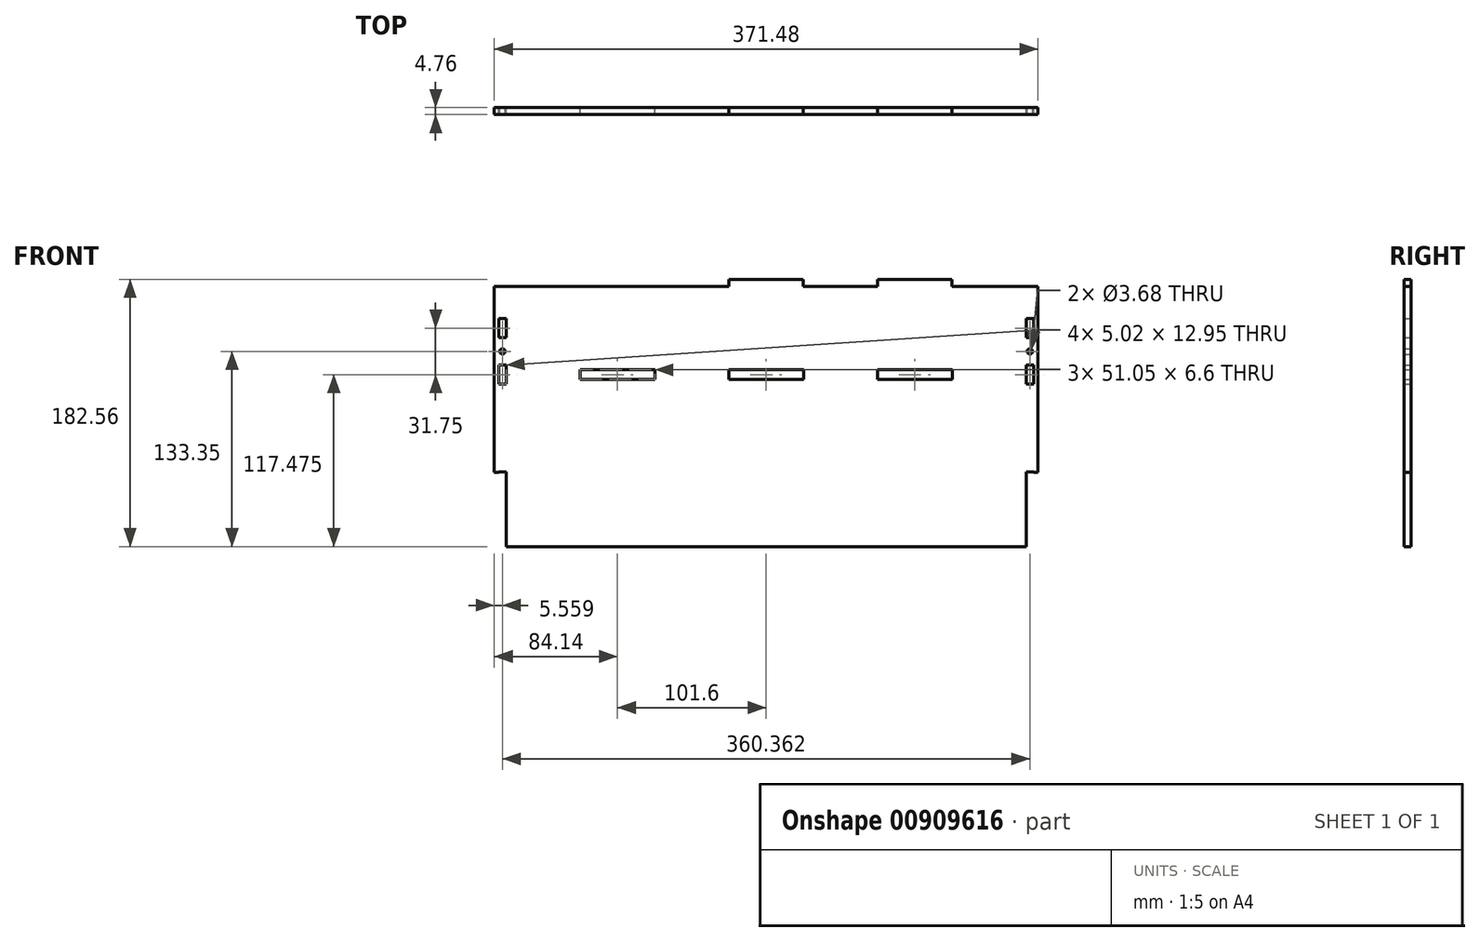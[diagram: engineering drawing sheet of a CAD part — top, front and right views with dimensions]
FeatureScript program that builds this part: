
annotation { "Feature Type Name" : "Feature", "Feature Type Description" : "" }
export const myFeature = defineFeature(function(context is Context, id is Id, definition is map)
    precondition{}
    {
        {
            var Q0;
            Q0=qCreatedBy(makeId("Front.planeOp"),FACE);
            var sketch = newSketch(context, id + "F0", { "sketchPlane" : qUnion([Q0])});
            skLineSegment(sketch, "E0.bottom", {"start": v(-182.56, 88.9) * mm, "end": v(182.56, 88.9) * mm});
            skLineSegment(sketch, "E0.top", {"start": v(-182.56, -88.9) * mm, "end": v(182.56, -88.9) * mm});
            skLineSegment(sketch, "E0.left", {"start": v(-182.56, 88.9) * mm, "end": v(-182.56, -88.9) * mm});
            skLineSegment(sketch, "E0.right", {"start": v(182.56, 88.9) * mm, "end": v(182.56, -88.9) * mm});
            skPoint(sketch, "E0.middle", {"position": v(0, 0) * mm});
            skLineSegment(sketch, "E1.0", {"start": v(-177.8, 88.9) * mm, "end": v(-177.8, -88.9) * mm, "construction": true});
            skLineSegment(sketch, "E2.0", {"start": v(177.8, 88.9) * mm, "end": v(177.8, -88.9) * mm, "construction": true});
            skLineSegment(sketch, "E3.bottom", {"start": v(-127, 31.75) * mm, "end": v(-76.2, 31.75) * mm});
            skLineSegment(sketch, "E3.top", {"start": v(-127, 25.4) * mm, "end": v(-76.2, 25.4) * mm});
            skLineSegment(sketch, "E3.left", {"start": v(-127, 31.75) * mm, "end": v(-127, 25.4) * mm});
            skLineSegment(sketch, "E3.right", {"start": v(-76.2, 31.75) * mm, "end": v(-76.2, 25.4) * mm});
            skLineSegment(sketch, "E4.0", {"start": v(-127.13, 31.88) * mm, "end": v(-76.07, 31.88) * mm});
            skLineSegment(sketch, "E4.1", {"start": v(-127.13, 31.88) * mm, "end": v(-127.13, 25.27) * mm});
            skLineSegment(sketch, "E4.2", {"start": v(-127.13, 25.27) * mm, "end": v(-76.07, 25.27) * mm});
            skLineSegment(sketch, "E4.3", {"start": v(-76.07, 31.88) * mm, "end": v(-76.07, 25.27) * mm});
            skLineSegment(sketch, "E5.1.0.0", {"start": v(-25.53, 31.88) * mm, "end": v(-25.53, 25.27) * mm});
            skLineSegment(sketch, "E5.1.0.1", {"start": v(-25.53, 31.88) * mm, "end": v(25.53, 31.88) * mm});
            skLineSegment(sketch, "E5.1.0.2", {"start": v(-25.53, 25.27) * mm, "end": v(25.53, 25.27) * mm});
            skLineSegment(sketch, "E5.1.0.3", {"start": v(25.4, 31.75) * mm, "end": v(25.4, 25.4) * mm});
            skLineSegment(sketch, "E5.1.0.4", {"start": v(-25.4, 31.75) * mm, "end": v(25.4, 31.75) * mm});
            skLineSegment(sketch, "E5.1.0.5", {"start": v(25.53, 31.88) * mm, "end": v(25.53, 25.27) * mm});
            skLineSegment(sketch, "E5.1.0.6", {"start": v(-25.4, 31.75) * mm, "end": v(-25.4, 25.4) * mm});
            skLineSegment(sketch, "E5.1.0.7", {"start": v(-25.4, 25.4) * mm, "end": v(25.4, 25.4) * mm});
            skLineSegment(sketch, "E5.2.0.0", {"start": v(76.07, 31.88) * mm, "end": v(76.07, 25.27) * mm});
            skLineSegment(sketch, "E5.2.0.1", {"start": v(76.07, 31.88) * mm, "end": v(127.13, 31.88) * mm});
            skLineSegment(sketch, "E5.2.0.2", {"start": v(76.07, 25.27) * mm, "end": v(127.13, 25.27) * mm});
            skLineSegment(sketch, "E5.2.0.3", {"start": v(127, 31.75) * mm, "end": v(127, 25.4) * mm});
            skLineSegment(sketch, "E5.2.0.4", {"start": v(76.2, 31.75) * mm, "end": v(127, 31.75) * mm});
            skLineSegment(sketch, "E5.2.0.5", {"start": v(127.13, 31.88) * mm, "end": v(127.13, 25.27) * mm});
            skLineSegment(sketch, "E5.2.0.6", {"start": v(76.2, 31.75) * mm, "end": v(76.2, 25.4) * mm});
            skLineSegment(sketch, "E5.2.0.7", {"start": v(76.2, 25.4) * mm, "end": v(127, 25.4) * mm});
            skLineSegment(sketch, "E5.direction1", {"start": v(-127, 25.4) * mm, "end": v(-25.4, 25.4) * mm, "construction": true});
            skLineSegment(sketch, "E6.bottom", {"start": v(-182.56, -88.9) * mm, "end": v(-177.8, -88.9) * mm});
            skLineSegment(sketch, "E6.top", {"start": v(-185.74, -38.1) * mm, "end": v(-177.8, -38.1) * mm});
            skLineSegment(sketch, "E6.left", {"start": v(-182.56, -88.9) * mm, "end": v(-182.56, -38.1) * mm});
            skLineSegment(sketch, "E6.right", {"start": v(-177.8, -88.9) * mm, "end": v(-177.8, -38.1) * mm});
            skLineSegment(sketch, "E7", {"start": v(0, 88.9) * mm, "end": v(0, -88.9) * mm, "construction": true});
            skLineSegment(sketch, "E8.MirrorCS", {"start": v(182.56, -88.9) * mm, "end": v(177.8, -88.9) * mm});
            skLineSegment(sketch, "E9.MirrorCS", {"start": v(182.56, -38.1) * mm, "end": v(177.8, -38.1) * mm});
            skLineSegment(sketch, "E10.MirrorCS", {"start": v(182.56, -88.9) * mm, "end": v(182.56, -38.1) * mm});
            skLineSegment(sketch, "E11.MirrorCS", {"start": v(177.8, -88.9) * mm, "end": v(177.8, -38.1) * mm});
            skLineSegment(sketch, "E12.0", {"start": v(-182.69, -89.03) * mm, "end": v(-177.67, -89.03) * mm});
            skLineSegment(sketch, "E12.1", {"start": v(-182.69, -89.03) * mm, "end": v(-182.69, -37.97) * mm});
            skLineSegment(sketch, "E12.2", {"start": v(-182.69, -37.97) * mm, "end": v(-177.67, -37.97) * mm});
            skLineSegment(sketch, "E12.3", {"start": v(-177.67, -89.03) * mm, "end": v(-177.67, -37.97) * mm});
            skLineSegment(sketch, "E13.bottom", {"start": v(-127, 88.9) * mm, "end": v(-76.2, 88.9) * mm});
            skLineSegment(sketch, "E13.top", {"start": v(-127, 93.66) * mm, "end": v(-76.2, 93.66) * mm});
            skLineSegment(sketch, "E13.left", {"start": v(-127, 88.9) * mm, "end": v(-127, 93.66) * mm});
            skLineSegment(sketch, "E13.right", {"start": v(-76.2, 88.9) * mm, "end": v(-76.2, 93.66) * mm});
            skLineSegment(sketch, "E14.1.0.0", {"start": v(-25.4, 93.66) * mm, "end": v(25.4, 93.66) * mm});
            skLineSegment(sketch, "E14.1.0.1", {"start": v(-25.4, 88.9) * mm, "end": v(25.4, 88.9) * mm});
            skLineSegment(sketch, "E14.1.0.2", {"start": v(-25.4, 88.9) * mm, "end": v(-25.4, 93.66) * mm});
            skLineSegment(sketch, "E14.1.0.3", {"start": v(25.4, 88.9) * mm, "end": v(25.4, 93.66) * mm});
            skLineSegment(sketch, "E14.2.0.0", {"start": v(76.2, 93.66) * mm, "end": v(127, 93.66) * mm});
            skLineSegment(sketch, "E14.2.0.1", {"start": v(76.2, 88.9) * mm, "end": v(127, 88.9) * mm});
            skLineSegment(sketch, "E14.2.0.2", {"start": v(76.2, 88.9) * mm, "end": v(76.2, 93.66) * mm});
            skLineSegment(sketch, "E14.2.0.3", {"start": v(127, 88.9) * mm, "end": v(127, 93.66) * mm});
            skLineSegment(sketch, "E14.direction1", {"start": v(-127, 88.9) * mm, "end": v(-25.4, 88.9) * mm, "construction": true});
            skLineSegment(sketch, "E15.MirrorCS", {"start": v(182.69, -89.03) * mm, "end": v(177.67, -89.03) * mm});
            skLineSegment(sketch, "E16.MirrorCS", {"start": v(182.69, -37.97) * mm, "end": v(177.67, -37.97) * mm});
            skLineSegment(sketch, "E17.MirrorCS", {"start": v(182.69, -89.03) * mm, "end": v(182.69, -37.97) * mm});
            skLineSegment(sketch, "E18.MirrorCS", {"start": v(177.67, -89.03) * mm, "end": v(177.67, -37.97) * mm});
            skCircle(sketch, "E19", {"center": v(-180.18, 44.45) * mm, "radius": 1.84 * mm});
            skCircle(sketch, "E20.MirrorC", {"center": v(180.18, 44.45) * mm, "radius": 1.84 * mm});
            skLineSegment(sketch, "E21.0", {"start": v(-185.74, 88.9) * mm, "end": v(-185.74, -38.1) * mm});
            skLineSegment(sketch, "E22", {"start": v(-185.74, 88.9) * mm, "end": v(-182.56, 88.9) * mm});
            skLineSegment(sketch, "E23.MirrorCS", {"start": v(185.74, -38.1) * mm, "end": v(177.8, -38.1) * mm});
            skLineSegment(sketch, "E24.MirrorCS", {"start": v(185.74, 88.9) * mm, "end": v(182.56, 88.9) * mm});
            skLineSegment(sketch, "E25.MirrorCS", {"start": v(185.74, 88.9) * mm, "end": v(185.74, -38.1) * mm});
            skLineSegment(sketch, "E26.bottom", {"start": v(-177.67, 35.05) * mm, "end": v(-182.69, 35.05) * mm});
            skLineSegment(sketch, "E26.top", {"start": v(-177.67, 22.1) * mm, "end": v(-182.69, 22.1) * mm});
            skLineSegment(sketch, "E26.left", {"start": v(-177.67, 35.05) * mm, "end": v(-177.67, 22.1) * mm});
            skLineSegment(sketch, "E26.right", {"start": v(-182.69, 35.05) * mm, "end": v(-182.69, 22.1) * mm});
            skPoint(sketch, "E26.middle", {"position": v(-180.18, 28.58) * mm});
            skPoint(sketch, "E26.middle.positionSnap0", {"position": v(-180.18, -37.97) * mm});
            skPoint(sketch, "E26.centerSnap0", {"position": v(-180.18, -37.97) * mm});
            skLineSegment(sketch, "E27", {"start": v(-185.74, 44.45) * mm, "end": v(-177.8, 44.45) * mm, "construction": true});
            skLineSegment(sketch, "E28.MirrorCS", {"start": v(-177.67, 53.85) * mm, "end": v(-182.69, 53.85) * mm});
            skPoint(sketch, "E29.MirrorP", {"position": v(-180.18, 60.33) * mm});
            skLineSegment(sketch, "E30.MirrorCS", {"start": v(-177.67, 66.8) * mm, "end": v(-182.69, 66.8) * mm});
            skLineSegment(sketch, "E31.MirrorCS", {"start": v(-182.69, 53.85) * mm, "end": v(-182.69, 66.8) * mm});
            skLineSegment(sketch, "E32.MirrorCS", {"start": v(-177.67, 53.85) * mm, "end": v(-177.67, 66.8) * mm});
            skLineSegment(sketch, "E33.MirrorCS", {"start": v(182.69, 53.85) * mm, "end": v(182.69, 66.8) * mm});
            skLineSegment(sketch, "E34.MirrorCS", {"start": v(177.67, 66.8) * mm, "end": v(182.69, 66.8) * mm});
            skLineSegment(sketch, "E35.MirrorCS", {"start": v(177.67, 53.85) * mm, "end": v(177.67, 66.8) * mm});
            skLineSegment(sketch, "E36.MirrorCS", {"start": v(177.67, 53.85) * mm, "end": v(182.69, 53.85) * mm});
            skPoint(sketch, "E37.MirrorP", {"position": v(180.18, 60.33) * mm});
            skLineSegment(sketch, "E38.MirrorCS", {"start": v(177.67, 35.05) * mm, "end": v(182.69, 35.05) * mm});
            skLineSegment(sketch, "E39.MirrorCS", {"start": v(182.69, 35.05) * mm, "end": v(182.69, 22.1) * mm});
            skLineSegment(sketch, "E40.MirrorCS", {"start": v(177.67, 35.05) * mm, "end": v(177.67, 22.1) * mm});
            skLineSegment(sketch, "E41.MirrorCS", {"start": v(177.67, 22.1) * mm, "end": v(182.69, 22.1) * mm});
            skPoint(sketch, "E42.MirrorP", {"position": v(180.18, 28.57) * mm});
            skSolve(sketch);
        }
        {
            var Q0;
            Q0=makeQuery(id+"F0.imprint","IMPRINT",FACE,{"disambiguationData":[TD([[makeQuery(id+"F0.imprint","IMPRINT",EDGE,{"derivedFrom":sQuery(id+"F0.wireOp",EDGE,"E0.bottom")}),-1.0]])]});
            var Q1;
            Q1=makeQuery(id+"F0.imprint","IMPRINT",FACE,{"disambiguationData":[TD([[makeQuery(id+"F0.imprint","IMPRINT",EDGE,{"derivedFrom":sQuery(id+"F0.wireOp",EDGE,"E13.bottom")}),1.0]])]});
            var Q2;
            Q2=makeQuery(id+"F0.imprint","IMPRINT",FACE,{"disambiguationData":[TD([[makeQuery(id+"F0.imprint","IMPRINT",EDGE,{"derivedFrom":sQuery(id+"F0.wireOp",EDGE,"E14.1.0.0")}),-1.0]])]});
            var Q3;
            Q3=makeQuery(id+"F0.imprint","IMPRINT",FACE,{"disambiguationData":[TD([[makeQuery(id+"F0.imprint","IMPRINT",EDGE,{"derivedFrom":sQuery(id+"F0.wireOp",EDGE,"E14.2.0.0")}),-1.0]])]});
            var Q4;
            {var subQ9=sQuery(id+"F0.wireOp",EDGE,"E22");Q4=makeQuery(id+"F0.imprint","IMPRINT",FACE,{"disambiguationData":[TD([[makeQuery(id+"F0.imprint","IMPRINT",EDGE,{"derivedFrom":subQ9}),-1.0]])]});}
            var Q5;
            {var subQ6=sQuery(id+"F0.wireOp",EDGE,"E24.MirrorCS");Q5=makeQuery(id+"F0.imprint","IMPRINT",FACE,{"disambiguationData":[TD([[makeQuery(id+"F0.imprint","IMPRINT",EDGE,{"derivedFrom":subQ6}),1.0]])]});}
            extrude(context, id + "F1", {"entities" : qUnion([Q0, Q1, Q2, Q3, Q4, Q5]), "depth" : 4.76 * mm, "offsetDistance" : 25.4 * mm});
        }
    });
